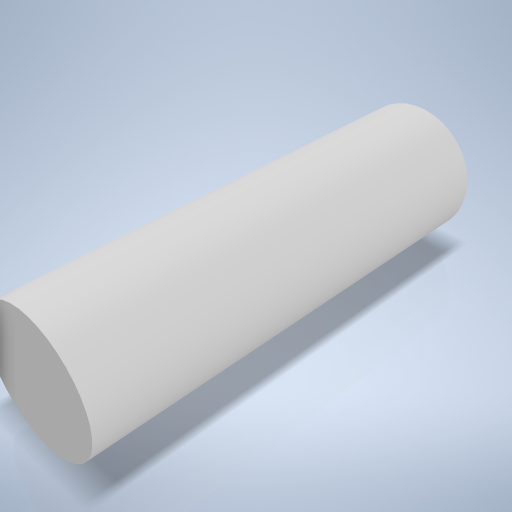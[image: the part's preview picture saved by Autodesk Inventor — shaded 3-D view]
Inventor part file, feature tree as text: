
AUTODESK INVENTOR PART (.ipt)
format: ipt  version: 2024.2 (Build 282272000, 272)  size: 220,672 bytes
history: native  units: mm
features: extrude x1, sketch x1
ambient origin geometry x8: Origin, YZ Plane, XZ Plane, XY Plane, X Axis, Y Axis, Z Axis, Center Point
bodies: Volumenkörper1 (feature_tree)
feature tree (2):
  extrude  "Extrusion1"  Depth=30.0mm TaperAngle=0.0deg
  sketch  "Skizze1"  dims[d0=9.0mm d1=30.0mm d2=0.0mm]
